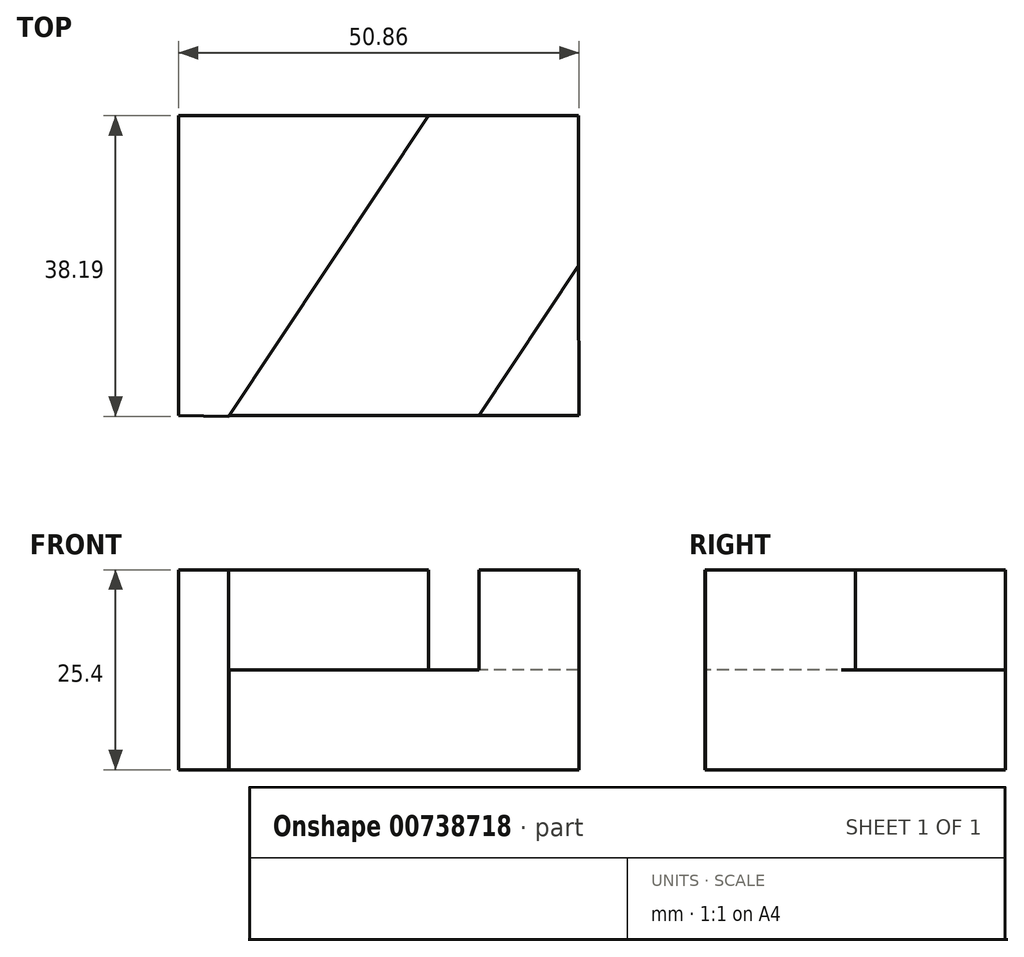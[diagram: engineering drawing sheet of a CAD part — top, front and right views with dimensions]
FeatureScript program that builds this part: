
annotation { "Feature Type Name" : "Feature", "Feature Type Description" : "" }
export const myFeature = defineFeature(function(context is Context, id is Id, definition is map)
    precondition{}
    {
        {
            var Q0;
            Q0=qCreatedBy(makeId("Front.planeOp"),FACE);
            var sketch = newSketch(context, id + "F0", { "sketchPlane" : qUnion([Q0])});
            skLineSegment(sketch, "E0", {"start": v(0, 12.7) * mm, "end": v(0, 0) * mm});
            skLineSegment(sketch, "E1", {"start": v(0, 0) * mm, "end": v(50.8, 0) * mm});
            skLineSegment(sketch, "E2", {"start": v(50.8, 0) * mm, "end": v(50.8, 12.7) * mm});
            skLineSegment(sketch, "E3", {"start": v(50.8, 12.7) * mm, "end": v(0, 12.7) * mm});
            skSolve(sketch);
        }
        {
            var Q0;
            Q0 = qSketchRegion(id + "F0", true);
            extrude(context, id + "F1", {"entities" : qUnion([Q0]), "depth" : 38.1 * mm, "offsetDistance" : 25.4 * mm});
        }
        {
            var Q0;
            Q0=qCreatedBy(makeId("Top.planeOp"),FACE);
            var sketch = newSketch(context, id + "F2", { "sketchPlane" : qUnion([Q0])});
            skLineSegment(sketch, "E4", {"start": v(6.35, -38.19) * mm, "end": v(31.75, 0) * mm});
            skLineSegment(sketch, "E5", {"start": v(31.75, 0) * mm, "end": v(0, 0) * mm});
            skLineSegment(sketch, "E6", {"start": v(0, 0) * mm, "end": v(0, -38.1) * mm});
            skLineSegment(sketch, "E7", {"start": v(0, -38.1) * mm, "end": v(6.35, -38.19) * mm});
            skSolve(sketch);
        }
        {
            var Q0;
            Q0 = qSketchRegion(id + "F2", true);
            extrude(context, id + "F3", {"entities" : qUnion([Q0]), "operationType" : NewBodyOperationType.ADD, "depth" : 25.4 * mm, "offsetDistance" : 25.4 * mm});
        }
        {
            var Q0;
            Q0=qCreatedBy(makeId("Top.planeOp"),FACE);
            var sketch = newSketch(context, id + "F4", { "sketchPlane" : qUnion([Q0])});
            skLineSegment(sketch, "E8", {"start": v(50.8, -19.05) * mm, "end": v(38.16, -38.1) * mm});
            skLineSegment(sketch, "E9", {"start": v(38.16, -38.1) * mm, "end": v(50.86, -38.1) * mm});
            skLineSegment(sketch, "E10", {"start": v(50.86, -38.1) * mm, "end": v(50.8, -19.05) * mm});
            skSolve(sketch);
        }
        {
            var Q0;
            Q0 = qSketchRegion(id + "F4", true);
            extrude(context, id + "F5", {"entities" : qUnion([Q0]), "operationType" : NewBodyOperationType.ADD, "depth" : 25.4 * mm, "offsetDistance" : 25.4 * mm});
        }
    });
